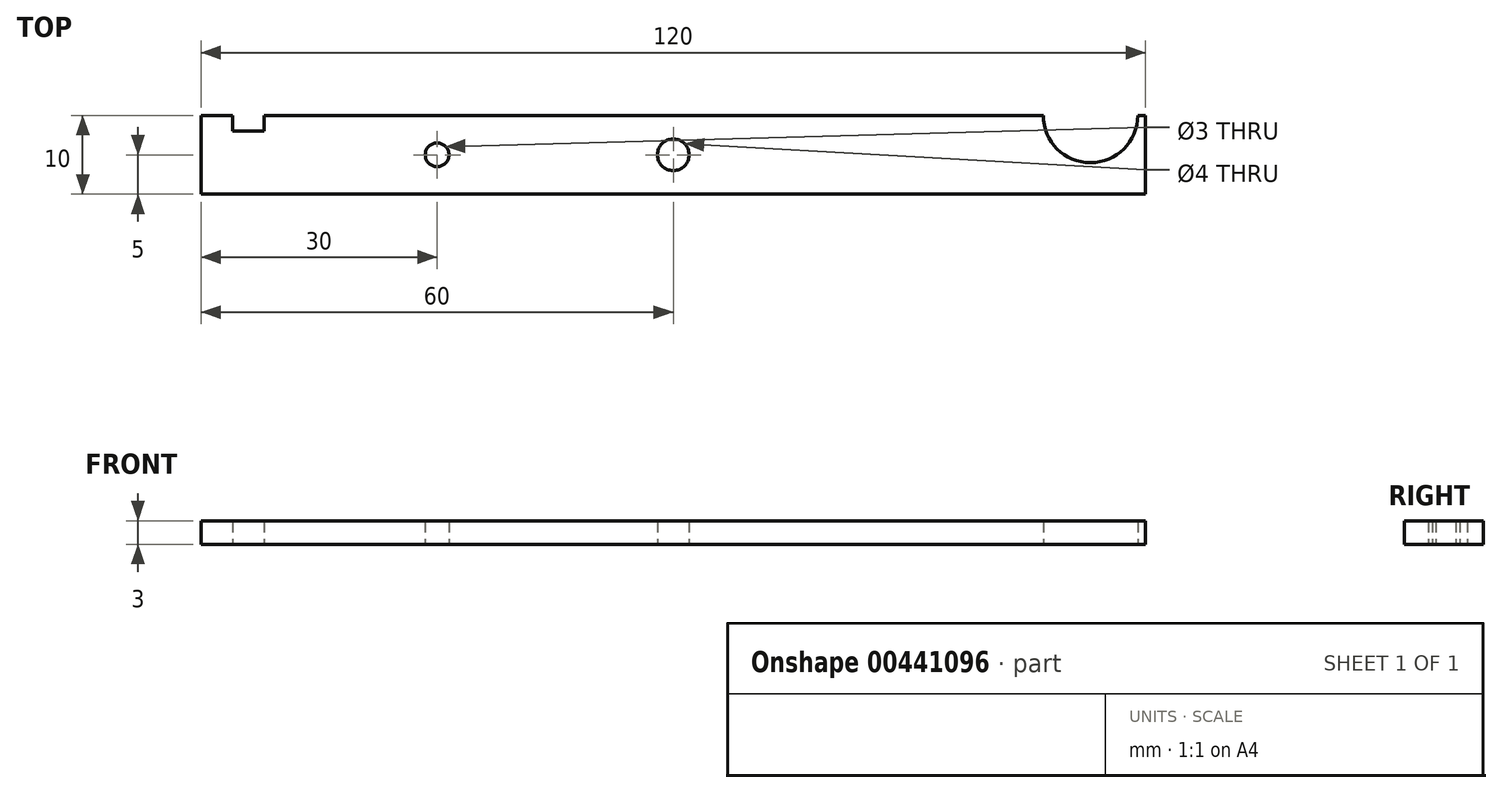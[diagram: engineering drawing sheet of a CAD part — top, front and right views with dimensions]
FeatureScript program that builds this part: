
annotation { "Feature Type Name" : "Feature", "Feature Type Description" : "" }
export const myFeature = defineFeature(function(context is Context, id is Id, definition is map)
    precondition{}
    {
        {
            var Q0;
            Q0=qCreatedBy(makeId("Top.planeOp"),FACE);
            var sketch = newSketch(context, id + "F0", { "sketchPlane" : qUnion([Q0])});
            skLineSegment(sketch, "E0.bottom", {"start": v(60, -5) * mm, "end": v(-60, -5) * mm});
            skLineSegment(sketch, "E0.top", {"start": v(60, 5) * mm, "end": v(-60, 5) * mm});
            skLineSegment(sketch, "E0.left", {"start": v(60, -5) * mm, "end": v(60, 5) * mm});
            skLineSegment(sketch, "E0.right", {"start": v(-60, -5) * mm, "end": v(-60, 5) * mm});
            skPoint(sketch, "E0.middle", {"position": v(0, 0) * mm});
            skCircle(sketch, "E1", {"center": v(0, 0) * mm, "radius": 7 * mm});
            skCircle(sketch, "E2", {"center": v(0, 0) * mm, "radius": 2 * mm});
            skLineSegment(sketch, "E3.bottom", {"start": v(-56, 5) * mm, "end": v(-52, 5) * mm});
            skLineSegment(sketch, "E3.top", {"start": v(-56, 3) * mm, "end": v(-52, 3) * mm});
            skLineSegment(sketch, "E3.left", {"start": v(-56, 5) * mm, "end": v(-56, 3) * mm});
            skLineSegment(sketch, "E3.right", {"start": v(-52, 5) * mm, "end": v(-52, 3) * mm});
            skCircle(sketch, "E4", {"center": v(53, 5) * mm, "radius": 6 * mm});
            skCircle(sketch, "E5", {"center": v(-30, 0) * mm, "radius": 1.5 * mm});
            skSolve(sketch);
        }
        {
            var Q0;
            {var subQ0=sQuery(id+"F0.wireOp",EDGE,"E0.right");Q0=makeQuery(id+"F0.imprint","IMPRINT",FACE,{"disambiguationData":[TD([[makeQuery(id+"F0.imprint","IMPRINT",EDGE,{"derivedFrom":subQ0}),-1.0]])]});}
            var Q1;
            Q1=makeQuery(id+"F0.imprint","IMPRINT",FACE,{"disambiguationData":[TD([[makeQuery(id+"F0.imprint","IMPRINT",EDGE,{"derivedFrom":sQuery(id+"F0.wireOp",EDGE,"E2")}),-1.0]])]});
            var Q2;
            {var subQ0=sQuery(id+"F0.wireOp",EDGE,"E1");var subQ1=sQuery(id+"F0.wireOp",EDGE,"E0.top");var subQ2=makeQuery(id+"F0.imprint","INTERSECT",VERTEX,{"disambiguationData":[OD(0.0)],"derivedFrom":[subQ1,subQ0]});Q2=makeQuery(id+"F0.imprint","IMPRINT",FACE,{"disambiguationData":[TD([[makeQuery(id+"F0.imprint","IMPRINT",EDGE,{"disambiguationData":[TD([[subQ2,-1.0]])],"derivedFrom":subQ1}),-1.0]])]});}
            var Q3;
            {var subQ0=sQuery(id+"F0.wireOp",EDGE,"E1");var subQ1=sQuery(id+"F0.wireOp",EDGE,"E0.bottom");var subQ2=makeQuery(id+"F0.imprint","INTERSECT",VERTEX,{"disambiguationData":[OD(0.0)],"derivedFrom":[subQ1,subQ0]});Q3=makeQuery(id+"F0.imprint","IMPRINT",FACE,{"disambiguationData":[TD([[makeQuery(id+"F0.imprint","IMPRINT",EDGE,{"disambiguationData":[TD([[subQ2,-1.0]])],"derivedFrom":subQ1}),1.0]])]});}
            var Q4;
            {var subQ0=sQuery(id+"F0.wireOp",EDGE,"E0.left");Q4=makeQuery(id+"F0.imprint","IMPRINT",FACE,{"disambiguationData":[TD([[makeQuery(id+"F0.imprint","IMPRINT",EDGE,{"derivedFrom":subQ0}),1.0]])]});}
            extrude(context, id + "F1", {"entities" : qUnion([Q0, Q1, Q2, Q3, Q4]), "depth" : 3 * mm});
        }
    });
